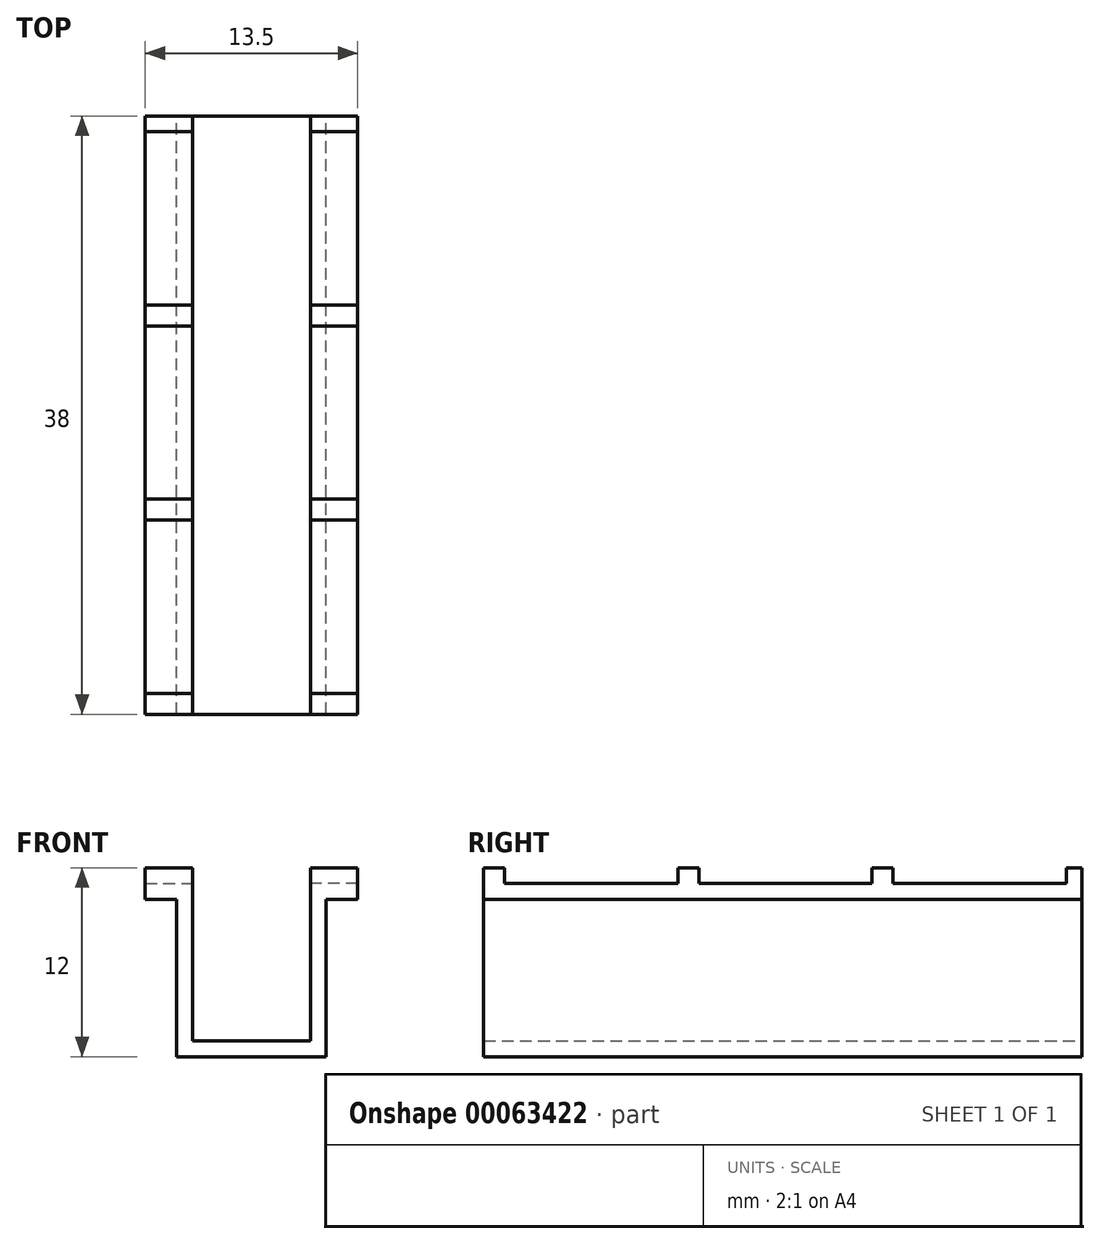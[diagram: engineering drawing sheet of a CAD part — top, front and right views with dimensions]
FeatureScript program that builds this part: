
annotation { "Feature Type Name" : "Feature", "Feature Type Description" : "" }
export const myFeature = defineFeature(function(context is Context, id is Id, definition is map)
    precondition{}
    {
        {
            var Q0;
            Q0=qCreatedBy(makeId("Front.planeOp"),FACE);
            var sketch = newSketch(context, id + "F0", { "sketchPlane" : qUnion([Q0])});
            skLineSegment(sketch, "E0", {"start": v(0, 0) * mm, "end": v(3, 0) * mm});
            skLineSegment(sketch, "E1", {"start": v(3, 0) * mm, "end": v(3, -10) * mm});
            skLineSegment(sketch, "E2", {"start": v(3, -10) * mm, "end": v(10.5, -10) * mm});
            skLineSegment(sketch, "E3", {"start": v(10.5, -10) * mm, "end": v(10.5, 0) * mm});
            skLineSegment(sketch, "E4.1.0.1", {"start": v(10.5, 0) * mm, "end": v(13.5, 0) * mm});
            skLineSegment(sketch, "E5.0", {"start": v(11.5, -1) * mm, "end": v(13.5, -1) * mm});
            skLineSegment(sketch, "E5.1", {"start": v(0, -1) * mm, "end": v(2, -1) * mm});
            skLineSegment(sketch, "E5.2", {"start": v(2, -1) * mm, "end": v(2, -11) * mm});
            skLineSegment(sketch, "E5.3", {"start": v(2, -11) * mm, "end": v(11.5, -11) * mm});
            skLineSegment(sketch, "E5.4", {"start": v(11.5, -11) * mm, "end": v(11.5, -1) * mm});
            skLineSegment(sketch, "E6", {"start": v(0, 0) * mm, "end": v(0, -1) * mm});
            skLineSegment(sketch, "E7", {"start": v(13.5, 0) * mm, "end": v(13.5, -1) * mm});
            skSolve(sketch);
        }
        {
            var Q0;
            Q0=qSketchRegion(id+"F0",true);
            extrude(context, id + "F1", {"entities" : qUnion([Q0]), "depth" : 100 * mm});
        }
        {
            var Q0;
            Q0=makeQuery(id+"F1.opExtrude","SWEPT_FACE",FACE,{"disambiguationData":[OSD([sQuery(id+"F0.wireOp",EDGE,"E0")])]});
            var sketch = newSketch(context, id + "F2", { "sketchPlane" : qUnion([Q0])});
            skLineSegment(sketch, "E8.bottom", {"start": v(0, 0) * mm, "end": v(3, 0) * mm});
            skLineSegment(sketch, "E8.top", {"start": v(0, -1.33) * mm, "end": v(3, -1.33) * mm});
            skLineSegment(sketch, "E8.left", {"start": v(0, 0) * mm, "end": v(0, -1.33) * mm});
            skLineSegment(sketch, "E8.right", {"start": v(3, 0) * mm, "end": v(3, -1.33) * mm});
            skLineSegment(sketch, "E9", {"start": v(6.75, -100) * mm, "end": v(6.75, -62.61) * mm, "construction": true});
            skPoint(sketch, "E10", {"position": v(6.75, -100) * mm});
            skLineSegment(sketch, "E11.MirrorCS", {"start": v(13.5, 0) * mm, "end": v(10.5, 0) * mm});
            skLineSegment(sketch, "E12.MirrorCS", {"start": v(13.5, -1.33) * mm, "end": v(10.5, -1.33) * mm});
            skLineSegment(sketch, "E13.MirrorCS", {"start": v(13.5, 0) * mm, "end": v(13.5, -1.33) * mm});
            skLineSegment(sketch, "E14.MirrorCS", {"start": v(10.5, 0) * mm, "end": v(10.5, -1.33) * mm});
            skLineSegment(sketch, "E15.0.1.0", {"start": v(0, -12.33) * mm, "end": v(3, -12.33) * mm});
            skLineSegment(sketch, "E15.0.1.1", {"start": v(13.5, -12.33) * mm, "end": v(10.5, -12.33) * mm});
            skLineSegment(sketch, "E15.0.1.2", {"start": v(13.5, -13.67) * mm, "end": v(10.5, -13.67) * mm});
            skLineSegment(sketch, "E15.0.1.3", {"start": v(0, -13.67) * mm, "end": v(3, -13.67) * mm});
            skLineSegment(sketch, "E15.0.1.4", {"start": v(3, -12.33) * mm, "end": v(3, -13.67) * mm});
            skLineSegment(sketch, "E15.0.1.5", {"start": v(10.5, -12.33) * mm, "end": v(10.5, -13.67) * mm});
            skLineSegment(sketch, "E15.0.1.6", {"start": v(13.5, -12.33) * mm, "end": v(13.5, -13.67) * mm});
            skLineSegment(sketch, "E15.0.1.7", {"start": v(0, -12.33) * mm, "end": v(0, -13.67) * mm});
            skLineSegment(sketch, "E15.0.2.0", {"start": v(0, -24.67) * mm, "end": v(3, -24.67) * mm});
            skLineSegment(sketch, "E15.0.2.1", {"start": v(13.5, -24.67) * mm, "end": v(10.5, -24.67) * mm});
            skLineSegment(sketch, "E15.0.2.2", {"start": v(13.5, -26) * mm, "end": v(10.5, -26) * mm});
            skLineSegment(sketch, "E15.0.2.3", {"start": v(0, -26) * mm, "end": v(3, -26) * mm});
            skLineSegment(sketch, "E15.0.2.4", {"start": v(3, -24.67) * mm, "end": v(3, -26) * mm});
            skLineSegment(sketch, "E15.0.2.5", {"start": v(10.5, -24.67) * mm, "end": v(10.5, -26) * mm});
            skLineSegment(sketch, "E15.0.2.6", {"start": v(13.5, -24.67) * mm, "end": v(13.5, -26) * mm});
            skLineSegment(sketch, "E15.0.2.7", {"start": v(0, -24.67) * mm, "end": v(0, -26) * mm});
            skLineSegment(sketch, "E15.0.3.0", {"start": v(0, -37) * mm, "end": v(3, -37) * mm});
            skLineSegment(sketch, "E15.0.3.1", {"start": v(13.5, -37) * mm, "end": v(10.5, -37) * mm});
            skLineSegment(sketch, "E15.0.3.2", {"start": v(13.5, -38.33) * mm, "end": v(10.5, -38.33) * mm});
            skLineSegment(sketch, "E15.0.3.3", {"start": v(0, -38.33) * mm, "end": v(3, -38.33) * mm});
            skLineSegment(sketch, "E15.0.3.4", {"start": v(3, -37) * mm, "end": v(3, -38.33) * mm});
            skLineSegment(sketch, "E15.0.3.5", {"start": v(10.5, -37) * mm, "end": v(10.5, -38.33) * mm});
            skLineSegment(sketch, "E15.0.3.6", {"start": v(13.5, -37) * mm, "end": v(13.5, -38.33) * mm});
            skLineSegment(sketch, "E15.0.3.7", {"start": v(0, -37) * mm, "end": v(0, -38.33) * mm});
            skLineSegment(sketch, "E15.0.4.0", {"start": v(0, -49.33) * mm, "end": v(3, -49.33) * mm});
            skLineSegment(sketch, "E15.0.4.1", {"start": v(13.5, -49.33) * mm, "end": v(10.5, -49.33) * mm});
            skLineSegment(sketch, "E15.0.4.2", {"start": v(13.5, -50.67) * mm, "end": v(10.5, -50.67) * mm});
            skLineSegment(sketch, "E15.0.4.3", {"start": v(0, -50.67) * mm, "end": v(3, -50.67) * mm});
            skLineSegment(sketch, "E15.0.4.4", {"start": v(3, -49.33) * mm, "end": v(3, -50.67) * mm});
            skLineSegment(sketch, "E15.0.4.5", {"start": v(10.5, -49.33) * mm, "end": v(10.5, -50.67) * mm});
            skLineSegment(sketch, "E15.0.4.6", {"start": v(13.5, -49.33) * mm, "end": v(13.5, -50.67) * mm});
            skLineSegment(sketch, "E15.0.4.7", {"start": v(0, -49.33) * mm, "end": v(0, -50.67) * mm});
            skLineSegment(sketch, "E15.0.5.0", {"start": v(0, -61.67) * mm, "end": v(3, -61.67) * mm});
            skLineSegment(sketch, "E15.0.5.1", {"start": v(13.5, -61.67) * mm, "end": v(10.5, -61.67) * mm});
            skLineSegment(sketch, "E15.0.5.2", {"start": v(13.5, -63) * mm, "end": v(10.5, -63) * mm});
            skLineSegment(sketch, "E15.0.5.3", {"start": v(0, -63) * mm, "end": v(3, -63) * mm});
            skLineSegment(sketch, "E15.0.5.4", {"start": v(3, -61.67) * mm, "end": v(3, -63) * mm});
            skLineSegment(sketch, "E15.0.5.5", {"start": v(10.5, -61.67) * mm, "end": v(10.5, -63) * mm});
            skLineSegment(sketch, "E15.0.5.6", {"start": v(13.5, -61.67) * mm, "end": v(13.5, -63) * mm});
            skLineSegment(sketch, "E15.0.5.7", {"start": v(0, -61.67) * mm, "end": v(0, -63) * mm});
            skLineSegment(sketch, "E15.0.6.0", {"start": v(0, -74) * mm, "end": v(3, -74) * mm});
            skLineSegment(sketch, "E15.0.6.1", {"start": v(13.5, -74) * mm, "end": v(10.5, -74) * mm});
            skLineSegment(sketch, "E15.0.6.2", {"start": v(13.5, -75.33) * mm, "end": v(10.5, -75.33) * mm});
            skLineSegment(sketch, "E15.0.6.3", {"start": v(0, -75.33) * mm, "end": v(3, -75.33) * mm});
            skLineSegment(sketch, "E15.0.6.4", {"start": v(3, -74) * mm, "end": v(3, -75.33) * mm});
            skLineSegment(sketch, "E15.0.6.5", {"start": v(10.5, -74) * mm, "end": v(10.5, -75.33) * mm});
            skLineSegment(sketch, "E15.0.6.6", {"start": v(13.5, -74) * mm, "end": v(13.5, -75.33) * mm});
            skLineSegment(sketch, "E15.0.6.7", {"start": v(0, -74) * mm, "end": v(0, -75.33) * mm});
            skLineSegment(sketch, "E15.0.7.0", {"start": v(0, -86.33) * mm, "end": v(3, -86.33) * mm});
            skLineSegment(sketch, "E15.0.7.1", {"start": v(13.5, -86.33) * mm, "end": v(10.5, -86.33) * mm});
            skLineSegment(sketch, "E15.0.7.2", {"start": v(13.5, -87.67) * mm, "end": v(10.5, -87.67) * mm});
            skLineSegment(sketch, "E15.0.7.3", {"start": v(0, -87.67) * mm, "end": v(3, -87.67) * mm});
            skLineSegment(sketch, "E15.0.7.4", {"start": v(3, -86.33) * mm, "end": v(3, -87.67) * mm});
            skLineSegment(sketch, "E15.0.7.5", {"start": v(10.5, -86.33) * mm, "end": v(10.5, -87.67) * mm});
            skLineSegment(sketch, "E15.0.7.6", {"start": v(13.5, -86.33) * mm, "end": v(13.5, -87.67) * mm});
            skLineSegment(sketch, "E15.0.7.7", {"start": v(0, -86.33) * mm, "end": v(0, -87.67) * mm});
            skLineSegment(sketch, "E15.0.8.0", {"start": v(0, -98.67) * mm, "end": v(3, -98.67) * mm});
            skLineSegment(sketch, "E15.0.8.1", {"start": v(13.5, -98.67) * mm, "end": v(10.5, -98.67) * mm});
            skLineSegment(sketch, "E15.0.8.2", {"start": v(13.5, -100) * mm, "end": v(10.5, -100) * mm});
            skLineSegment(sketch, "E15.0.8.3", {"start": v(0, -100) * mm, "end": v(3, -100) * mm});
            skLineSegment(sketch, "E15.0.8.4", {"start": v(3, -98.67) * mm, "end": v(3, -100) * mm});
            skLineSegment(sketch, "E15.0.8.5", {"start": v(10.5, -98.67) * mm, "end": v(10.5, -100) * mm});
            skLineSegment(sketch, "E15.0.8.6", {"start": v(13.5, -98.67) * mm, "end": v(13.5, -100) * mm});
            skLineSegment(sketch, "E15.0.8.7", {"start": v(0, -98.67) * mm, "end": v(0, -100) * mm});
            skLineSegment(sketch, "E15.direction1", {"start": v(0, -1.33) * mm, "end": v(25, -1.33) * mm, "construction": true});
            skLineSegment(sketch, "E15.direction2", {"start": v(0, -1.33) * mm, "end": v(0, -13.67) * mm, "construction": true});
            skSolve(sketch);
        }
        {
            var Q0;
            Q0=qSketchRegion(id+"F2",true);
            extrude(context, id + "F3", {"entities" : qUnion([Q0]), "operationType" : NewBodyOperationType.ADD, "depth" : 1 * mm});
        }
        {
            var Q0;
            Q0=qCreatedBy(makeId("Top.planeOp"),FACE);
            var sketch = newSketch(context, id + "F4", { "sketchPlane" : qUnion([Q0])});
            skLineSegment(sketch, "E16.bottom", {"start": v(0, 0) * mm, "end": v(23.25, 0) * mm});
            skLineSegment(sketch, "E16.top", {"start": v(0, -62) * mm, "end": v(23.25, -62) * mm});
            skLineSegment(sketch, "E16.left", {"start": v(0, 0) * mm, "end": v(0, -62) * mm});
            skLineSegment(sketch, "E16.right", {"start": v(23.25, 0) * mm, "end": v(23.25, -62) * mm});
            skSolve(sketch);
        }
        {
            var Q0;
            Q0 = qSketchRegion(id + "F4", true);
            extrude(context, id + "F5", {"entities" : qUnion([Q0]), "operationType" : NewBodyOperationType.REMOVE, "endBound" : BoundingType.THROUGH_ALL, "depth" : 25 * mm, "hasSecondDirection" : true, "secondDirectionBound" : SecondDirectionBoundingType.THROUGH_ALL, "secondDirectionOppositeDirection" : true, "secondDirectionDepth" : 25 * mm});
        }
    });
